# Revit family: Tyco_FireDtctnAlmCtrlIndctEquip_FireClass-AddressableOpticalSmokeDetector
name_source: partatom
category: Fire Alarm Devices
revit_build: Autodesk Revit MEP 2013 (Build: 20120221_2030(x64)
units: mm (PartAtom-declared; Revit-internal decimal feet)

## types (1)
- FC460P
    AlarmCurrent = 3.3mA
    AssetType = Moveable
    BIMObjectName = Tyco_FireDtctnAlmCtrlIndctEquip_FireClass-AddressableOpticalSmokeDetector-FC460P
    Brand = FireClass
    Category = Ee_40_15_75
    Color = White
    Default Elevation = 1200 mm
    Description = FC460P Addressable Optical Smoke Detector without built in- line isolator and IR Communication Link
    Detector Color = Plastic Material White
    DetectorType = Smoke Detector
    DeviceBases = 4B_Detector Base/4B-I_Isolator Detector Base
    DurationUnit = Year
    Features = Addressable Optical Smoke Sensor
    HasBuiltInAlarm = No
    HasProtectiveEarth = No
    IPCode = IP44
    IfcExportAs = IfcSensorType
    IfcExportType = SMOKESENSOR
    IfcTypeObject = IfcBuildingElementProxy
    Manufacturer = Tyco Fire Protection Products
    ManufacturerName = Tyco Fire Protection Products
    ManufacturerURL = www.fireclass.net
    Material = Flame Retardant-FR3010 ‘BAYBLEND'
    Model = FC460P
    ModelNumber = FC460P
    NBSDescription = Fire detection and alarm control and indicating equipment (CIE)
    NBSReference = 90-75-30/380
    Name = FC460P-Addressable Optical Smoke Detector without built in- line isolator
    NominalDiameter = 108 mm
    NominalHeight = 42 mm
    NominalLength = 108 mm
    NominalVoltage = 40 V DC
    NominalWidth = 108 mm
    NumberOfPoles = 0
    OperationTemperatureRange = -25 °C to +70 °C
    PhaseAngle = 0.00°
    ProductCodes = 516.460.502
    ProductInformation = https://fireclass.co.uk
    ProductSpecification = FC460P Addressable Optical Smoke Detector without built in- line isolator and IR Communication Link
    QuiescentCurrent = 250μA
    RelativeHumidity = 95%(non-condensing)
    ShortCircuitIsolators = No
    StorageTemperature = -40 °C to +80 °C
    Type Comments = Only 4B_Detector or 4B-I_Isolator Detector Bases can be used with FC460P Detector
    URL = https://fireclass.co.uk
    Uniclass2 = Ee_40_15_75
    UsageCurrent = 250μA
    Version = 1
    Voltage = 20 – 40 VDC
    WarrantyDurationLabor = 1.5 years
    WarrantyDurationParts = 1.5 years
    WarrantyDurationUnit = Year
    Weight = (Excluding Base) 76g

## geometry (parser evidence)
native form markers: Sweep x4
no freeform markers — native parametric forms only
